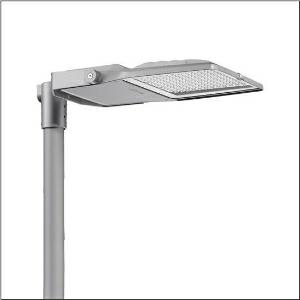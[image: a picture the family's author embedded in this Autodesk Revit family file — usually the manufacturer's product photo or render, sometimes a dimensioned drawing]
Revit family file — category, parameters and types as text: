
# Revit family: floodlight_fl_21_iq_midi___pl61_5xa7782e4c3a_83e0
name_source: partatom
category: Lighting Fixtures
units: mm (PartAtom-declared; Revit-internal decimal feet)

## family parameters
Cut with Voids When Loaded = No
Host = Face
Light Source = No
Part Type = Normal
Room Calculation Point = No
Round Connector Dimension = Use Diameter
Shared = No

## types (1)
- --- (1 x LED, 27490 lm, 208.1 W, 4000K)
    Apparent Load = 208 VA
    CIE Flux Codes = 33 65 98 100 100
    Color Rendering = 70
    Color Temperature = 4000K
    Default Elevation = 1800 mm
    Description = Floodlight FL 21 iQ midi, floodlight, primary light control with lens, of PMMA, primary optical cover: protective disc, of toughened safety glass, transparent, light distribution: PL61, light emission: direct distribution, installation type: surface-mounted, LED, High Power LED, rated luminous flux: 27.490lm, luminous efficacy: 132lm/W, light colour: 740, colour temperature: 4000K, control gear: iQ Street-Remote/DALI, control: optimised constant luminous flux control (CLO 2.0), Desk-Remote (wireless, voltage-free reading and setting of iQ features in the workshop via application-optimized NFC function/RFID function), Smart-Wire, Night-Set, Temp-Guard, Auto-Match, Street-Remote, with terminal, 6-pole, mains connection: 220..240V, AC, 50/60Hz, start of lifetime: 208W, end of service life: 227W, reduction: 90W, luminaire housing, of diecast aluminium, powder-coated, Siteco® metallic grey (DB 702S), corrosivity category C5 mid according to DIN EN ISO 12944, suitable for swimming pools, chlorine-resistant, sealing non-destructively replaceable, please order mast flange separately, mast bracket, of steel, galvanised, powder-coated, Siteco® metallic grey (DB 702S), protection rating (complete): IP66, insulation class (complete): insulation class II (safety insulation), certification: CE, ENEC, VDE, protection symbol: D, impact resistance: IK08, permissible operating ambient temperature: -40..+40°C, permissible operating ambient temperature for outdoor applications: -40..+50°C, standard: DIN EN 12944, LABS conformity tested according to VDMA 24364:2018-05, packaging unit: 1 piece

Light Distribution: PL61
    Height = 76 mm
    Lamp = 1 x LED
    Lamp Light Flux = 27490 lm
    Lamp Power = 208.1 W
    Lamp count = 1
    Length = 657 mm
    Luminous efficacy = 132 lm/W
    Manufacturer = Siteco
    ModVariant = No
    Model = 5XA7782E4C3A
    Number of Poles = 1
    OnlyDefault = Yes
    Power Factor = 1
    Product Name = Floodlight FL 21 iQ midi | PL61
    Product group = floodlight | pylon annexe
    ProductGroupID = 6200
    Protection Class = Protection class II
    Protection Degree = IP 66
    RLX_Detail_Level = 1
    RLX_Emergency_Light_Flux = 0 lm
    RLX_Emergency_Type = 0
    RLX_Emergency_Type_DB = No
    RlxData = <blob elided: 153597 chars, md5=a78691b3>
    Socket = socket
    Standby Power = 0 W
    System Light Flux = 27490 lm
    System Power = 208 W
    Type Comments = factory setting: luminous flux: 100 % | dim-lin: 254 | 710 mA
    Type Image = l_1007123.jpg
    URL = http://relux.com
    VarID = @adj_108634
    Voltage = 0 V
    Weight = 0.00 kg
    Width = 442 mm

## geometry (parser evidence)
native form markers: Blend x4, Sweep x14
no freeform markers — native parametric forms only
